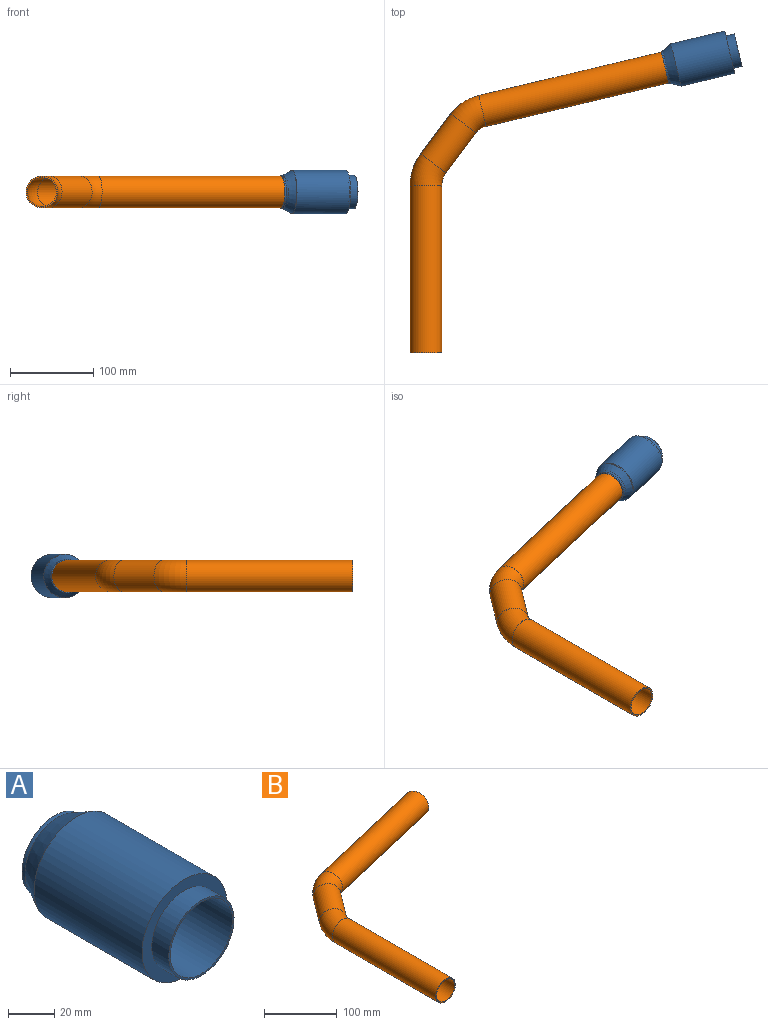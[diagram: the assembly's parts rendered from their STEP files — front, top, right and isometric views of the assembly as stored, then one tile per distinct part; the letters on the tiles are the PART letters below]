
ASSEMBLY  parts=2 mates=1
PART A: 13 faces, bbox 52x90x52 mm
  f0: cylinder r=20mm len=73.29mm, axis (0,1,0), area 9159.5mm2, adj f1,f3,f4
  f1: cone r=24.5mm half-angle=27.5deg, axis (0,-1,0), area 1362mm2, adj f0,f2
  f2: cylinder r=24.5mm len=64.65mm, axis (0,1,0), area 9952mm2, adj f1,f3
  f3: plane 49x49mm, normal (0,1,0), area 629.1mm2, adj f0,f2
  f4: cylinder r=4mm len=8mm, axis (0,0,-1), area 25.4mm2, adj f0,f5
  f5: cylinder r=19mm len=90mm, axis (0,1,0), area 10693.9mm2, adj f4,f9,f12
  f6: cone r=19mm half-angle=27.5deg, axis (0,-1,0), area 1877.2mm2, adj f7,f11
  f7: cylinder r=26mm len=66.15mm, axis (0,1,0), area 10806.4mm2, adj f6,f8
  f8: plane 52x52mm, normal (0,-1,0), area 867.1mm2, adj f7,f10
  f9: plane 40x40mm, normal (0,-1,0), area 122.5mm2, adj f5,f10
  f10: cylinder r=20mm len=40mm, axis (0,1,0), area 1308mm2, adj f8,f9
  f11: cylinder r=20mm len=40mm, axis (0,1,0), area 241.3mm2, adj f6,f12
  f12: plane 40x40mm, normal (0,1,0), area 122.5mm2, adj f5,f11
PART B: 12 faces, bbox 315.3x360.5x38 mm
  f0: cylinder r=17.5mm len=200mm, axis (0,1,0), area 21991.1mm2, adj f1,f5
  f1: torus R=45mm, axis (0,0,-1), area 3184mm2, adj f0,f2
  f2: cylinder r=17.5mm len=69mm, axis (0.6,0.8,0), area 6597.3mm2, adj f1,f3
  f3: torus R=40mm, axis (0,0,-1), area 3051.4mm2, adj f2,f4
  f4: cylinder r=17.5mm len=226.99mm, axis (0.97,0.23,0), area 24740mm2, adj f3,f6
  f5: plane 38x38mm, normal (0,-1,0), area 172mm2, adj f0,f7
  f6: plane 38x36.97mm, normal (0.97,0.23,0), area 172mm2, adj f4,f11
  f7: cylinder r=19mm len=200mm, axis (0,1,0), area 23876.1mm2, adj f5,f8
  f8: torus R=45mm, axis (0,0,-1), area 3457mm2, adj f7,f9
  f9: cylinder r=19mm len=70.8mm, axis (0.6,0.8,0), area 7162.8mm2, adj f8,f10
  f10: torus R=40mm, axis (0,0,-1), area 3312.9mm2, adj f9,f11
  f11: cylinder r=19mm len=227.69mm, axis (0.97,0.23,0), area 26860.6mm2, adj f6,f10
PLACE A rot(axis=(0,0,1),103.4deg) t=(168.06,182.81,25.9)mm
PLACE B t=(-30.52,-159.17,25.9)mm
MATE fastened A.f0 <-> B.f4  axis (-0.97,-0.23,0) through (168.06,182.81,25.9)mm
